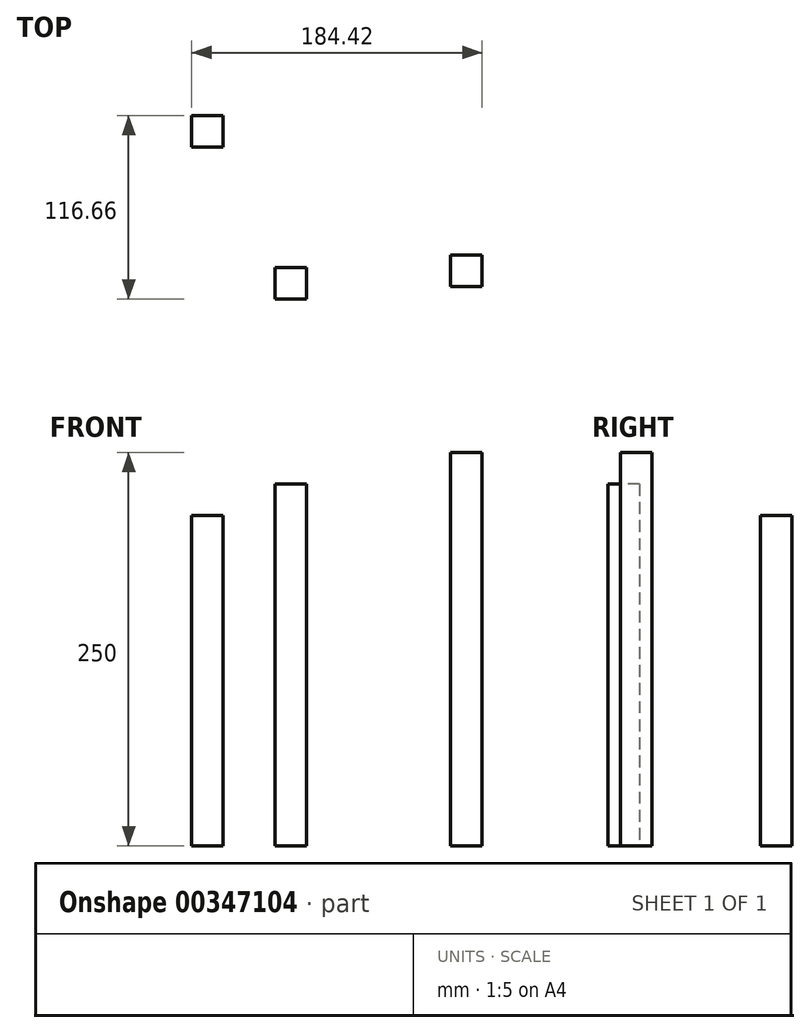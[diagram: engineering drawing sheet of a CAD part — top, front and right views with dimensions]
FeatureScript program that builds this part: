
annotation { "Feature Type Name" : "Feature", "Feature Type Description" : "" }
export const myFeature = defineFeature(function(context is Context, id is Id, definition is map)
    precondition{}
    {
        {
            var Q0;
            Q0=qCreatedBy(makeId("Top.planeOp"),FACE);
            var sketch = newSketch(context, id + "F0", { "sketchPlane" : qUnion([Q0])});
            skLineSegment(sketch, "E0.bottom", {"start": v(43.17, -48.05) * mm, "end": v(63.17, -48.05) * mm});
            skLineSegment(sketch, "E0.top", {"start": v(43.17, -68.05) * mm, "end": v(63.17, -68.05) * mm});
            skLineSegment(sketch, "E0.left", {"start": v(43.17, -48.05) * mm, "end": v(43.17, -68.05) * mm});
            skLineSegment(sketch, "E0.right", {"start": v(63.17, -48.05) * mm, "end": v(63.17, -68.05) * mm});
            skPoint(sketch, "E0.middle", {"position": v(53.17, -58.05) * mm});
            skLineSegment(sketch, "E1.bottom", {"start": v(-68.34, -55.88) * mm, "end": v(-48.34, -55.88) * mm});
            skLineSegment(sketch, "E1.top", {"start": v(-68.34, -75.88) * mm, "end": v(-48.34, -75.88) * mm});
            skLineSegment(sketch, "E1.left", {"start": v(-68.34, -55.88) * mm, "end": v(-68.34, -75.88) * mm});
            skLineSegment(sketch, "E1.right", {"start": v(-48.34, -55.88) * mm, "end": v(-48.34, -75.88) * mm});
            skPoint(sketch, "E1.middle", {"position": v(-58.34, -65.88) * mm});
            skLineSegment(sketch, "E2.bottom", {"start": v(-121.25, 40.78) * mm, "end": v(-101.25, 40.78) * mm});
            skLineSegment(sketch, "E2.top", {"start": v(-121.25, 20.78) * mm, "end": v(-101.25, 20.78) * mm});
            skLineSegment(sketch, "E2.left", {"start": v(-121.25, 40.78) * mm, "end": v(-121.25, 20.78) * mm});
            skLineSegment(sketch, "E2.right", {"start": v(-101.25, 40.78) * mm, "end": v(-101.25, 20.78) * mm});
            skPoint(sketch, "E2.middle", {"position": v(-111.25, 30.78) * mm});
            skSolve(sketch);
        }
        {
            var Q0;
            Q0=makeQuery(id+"F0.imprint","IMPRINT",FACE,{"disambiguationData":[TD([[makeQuery(id+"F0.imprint","IMPRINT",EDGE,{"derivedFrom":sQuery(id+"F0.wireOp",EDGE,"E0.bottom")}),-1.0]])]});
            extrude(context, id + "F1", {"entities" : qUnion([Q0]), "depth" : 250 * mm});
        }
        {
            var Q0;
            Q0=makeQuery(id+"F0.imprint","IMPRINT",FACE,{"disambiguationData":[TD([[makeQuery(id+"F0.imprint","IMPRINT",EDGE,{"derivedFrom":sQuery(id+"F0.wireOp",EDGE,"E1.bottom")}),-1.0]])]});
            extrude(context, id + "F2", {"entities" : qUnion([Q0]), "depth" : 230 * mm});
        }
        {
            var Q0;
            Q0=makeQuery(id+"F0.imprint","IMPRINT",FACE,{"disambiguationData":[TD([[makeQuery(id+"F0.imprint","IMPRINT",EDGE,{"derivedFrom":sQuery(id+"F0.wireOp",EDGE,"E2.bottom")}),-1.0]])]});
            extrude(context, id + "F3", {"entities" : qUnion([Q0]), "depth" : 210 * mm});
        }
    });
